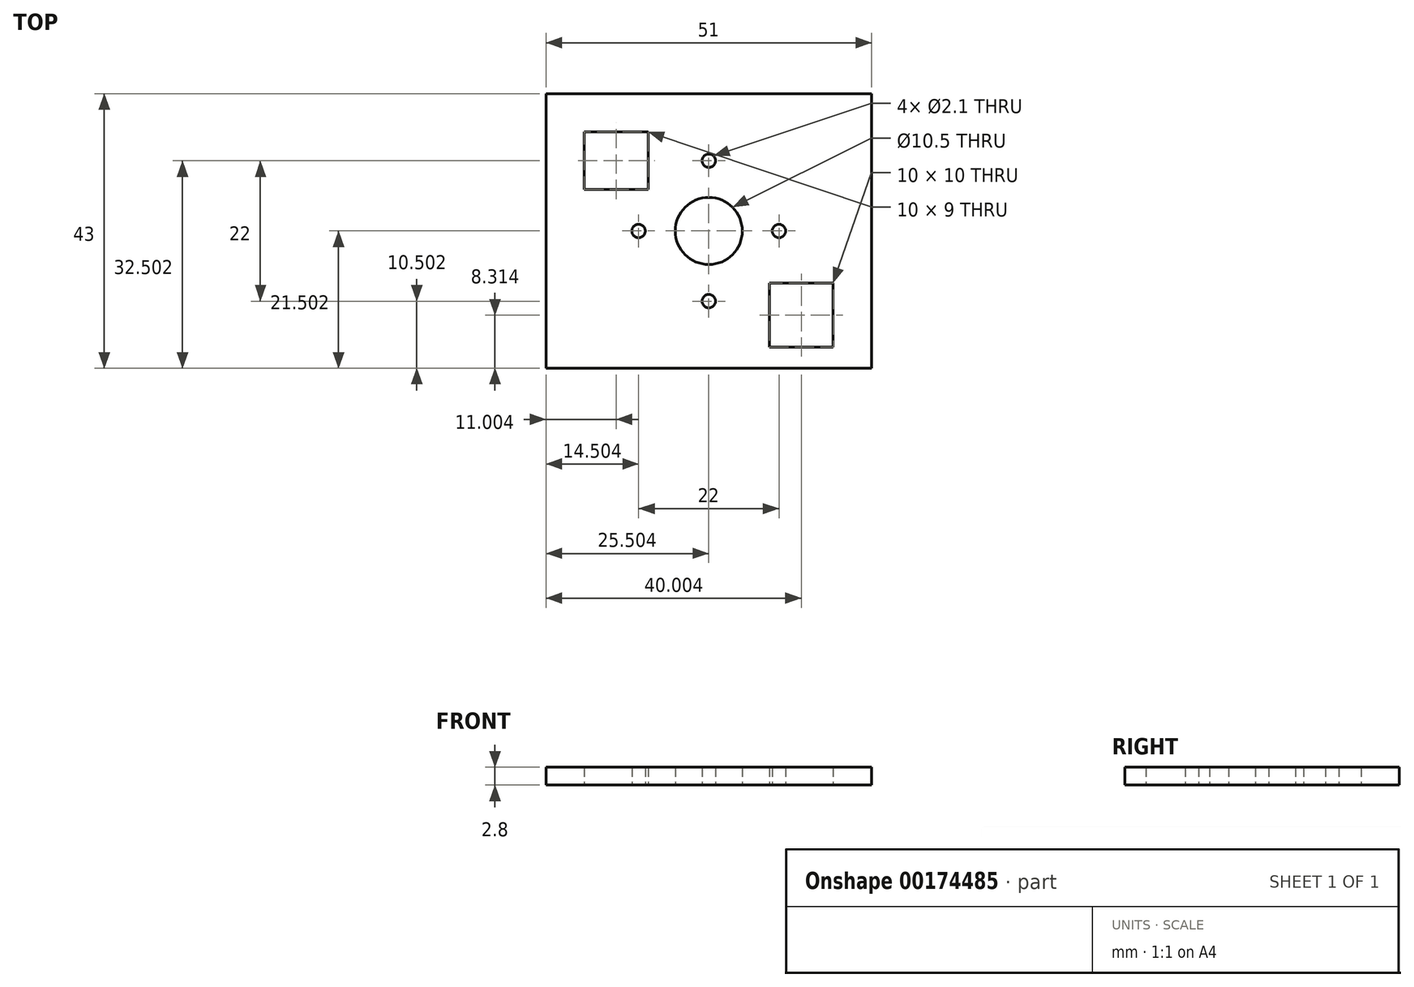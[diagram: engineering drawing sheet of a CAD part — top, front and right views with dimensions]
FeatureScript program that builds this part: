
annotation { "Feature Type Name" : "Feature", "Feature Type Description" : "" }
export const myFeature = defineFeature(function(context is Context, id is Id, definition is map)
    precondition{}
    {
        {
            var Q0;
            Q0=qCreatedBy(makeId("Top.planeOp"),FACE);
            var sketch = newSketch(context, id + "F0", { "sketchPlane" : qUnion([Q0])});
            skLineSegment(sketch, "E0.bottom", {"start": v(-62.38, 51) * mm, "end": v(-11.38, 51) * mm});
            skLineSegment(sketch, "E0.top", {"start": v(-62.38, 8) * mm, "end": v(-11.38, 8) * mm});
            skLineSegment(sketch, "E0.left", {"start": v(-62.38, 51) * mm, "end": v(-62.38, 8) * mm});
            skLineSegment(sketch, "E0.right", {"start": v(-11.38, 51) * mm, "end": v(-11.38, 8) * mm});
            skLineSegment(sketch, "E1", {"start": v(-36.88, 51) * mm, "end": v(-36.88, 8) * mm, "construction": true});
            skLineSegment(sketch, "E2", {"start": v(-11.38, 29.5) * mm, "end": v(-62.38, 29.5) * mm, "construction": true});
            skCircle(sketch, "E3", {"center": v(-36.88, 29.5) * mm, "radius": 5.25 * mm});
            skCircle(sketch, "E4", {"center": v(-36.88, 29.5) * mm, "radius": 11 * mm, "construction": true});
            skCircle(sketch, "E5", {"center": v(-25.88, 29.5) * mm, "radius": 1.05 * mm});
            skCircle(sketch, "E6", {"center": v(-36.88, 40.5) * mm, "radius": 1.05 * mm});
            skCircle(sketch, "E7", {"center": v(-47.88, 29.5) * mm, "radius": 1.05 * mm});
            skCircle(sketch, "E8", {"center": v(-36.88, 18.5) * mm, "radius": 1.05 * mm});
            skCircle(sketch, "E9", {"center": v(-62.38, 51) * mm, "radius": 6 * mm, "construction": true});
            skCircle(sketch, "E10", {"center": v(-11.38, 8) * mm, "radius": 6 * mm, "construction": true});
            skLineSegment(sketch, "E11", {"start": v(-62.38, 45) * mm, "end": v(-11.38, 45) * mm, "construction": true});
            skLineSegment(sketch, "E12", {"start": v(-56.38, 51) * mm, "end": v(-56.38, 8) * mm, "construction": true});
            skLineSegment(sketch, "E13", {"start": v(-11.38, 14) * mm, "end": v(-62.38, 14) * mm, "construction": true});
            skLineSegment(sketch, "E14", {"start": v(-17.38, 8) * mm, "end": v(-17.38, 51) * mm, "construction": true});
            skLineSegment(sketch, "E15.bottom", {"start": v(-56.38, 45) * mm, "end": v(-46.38, 45) * mm});
            skLineSegment(sketch, "E15.top", {"start": v(-56.38, 36) * mm, "end": v(-46.38, 36) * mm});
            skLineSegment(sketch, "E15.left", {"start": v(-56.38, 45) * mm, "end": v(-56.38, 36) * mm});
            skLineSegment(sketch, "E15.right", {"start": v(-46.38, 45) * mm, "end": v(-46.38, 36) * mm});
            skLineSegment(sketch, "E16.bottom", {"start": v(-17.38, 11.3) * mm, "end": v(-27.38, 11.3) * mm});
            skLineSegment(sketch, "E16.top", {"start": v(-17.38, 21.3) * mm, "end": v(-27.38, 21.3) * mm});
            skLineSegment(sketch, "E16.left", {"start": v(-17.38, 11.3) * mm, "end": v(-17.38, 21.3) * mm});
            skLineSegment(sketch, "E16.right", {"start": v(-27.38, 11.3) * mm, "end": v(-27.38, 21.3) * mm});
            skSolve(sketch);
        }
        {
            var Q0;
            Q0=makeQuery(id+"F0.imprint","IMPRINT",FACE,{"disambiguationData":[TD([[makeQuery(id+"F0.imprint","IMPRINT",EDGE,{"derivedFrom":sQuery(id+"F0.wireOp",EDGE,"E0.bottom")}),-1.0]])]});
            extrude(context, id + "F1", {"entities" : qUnion([Q0]), "depth" : 2.8 * mm});
        }
    });
